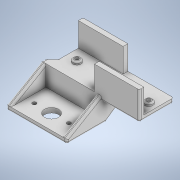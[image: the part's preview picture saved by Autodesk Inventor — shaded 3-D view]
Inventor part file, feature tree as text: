
AUTODESK INVENTOR PART (.ipt)
format: ipt  version: 2022 (Build 260153000, 153)  size: 325,120 bytes
history: native  units: in
note: dims shown in document units (in); Inventor stores cm internally (conversion verified against a paired STEP export)
features: extrude x9, sketch x9, chamfer x2, fillet x1
ambient origin geometry x8: Origin, YZ Plane, XZ Plane, XY Plane, X Axis, Y Axis, Z Axis, Center Point
bodies: Solid1 (feature_tree)
feature tree (21):
  extrude  "Extrusion1"  Depth=1.4331in
  extrude  "Extrusion2"  Depth=0.1969in
  extrude  "Extrusion3"  Depth=0.1969in
  extrude  "Extrusion5"  Depth=1.0in TaperAngle=0.0deg
  chamfer  "Chamfer1"  Distance=0.1181in
  extrude  "Extrusion6"  Depth=0.3937in
  extrude  "Extrusion7"  Depth=0.3937in
  extrude  "Extrusion8"  Depth=0.3937in
  chamfer  "Chamfer2"  Distance=0.0984in
  extrude  "Extrusion9"  Depth=0.0787in TaperAngle=45.0deg
  fillet  "Fillet2"  Radius=2.5197in
  extrude  "Extrusion10"  Depth=0.1969in
  sketch  "Sketch1"  dims[d0=3.7795in d1=1.4331in]
  sketch  "Sketch2"  dims[d2=0.1969in d3=0.0in d4=1.8701in]
  sketch  "Sketch3"  dims[d5=0.1969in d6=1.8701in]
  sketch  "Sketch5"  dims[d7=0.1969in d8=1.0in d9=0.0in]
  sketch  "Sketch6"  dims[d10=0.3406in]
  sketch  "Sketch7"  dims[d11=0.3406in]
  sketch  "Sketch8"  dims[d12=0.3406in]
  sketch  "Sketch9"  dims[d13=0.3406in d14=0.1181in d15=0.0in]
  sketch  "Sketch10"  dims[d22=0.2362in d23=0.2362in d24=0.2362in d25=0.2362in d26=0.0984in d27=0.0in d28=0.0591in d29=0.0787in d30=45.0deg d33=2.5197in d34=0.1969in d35=0.1969in d36=0.1969in d37=0.1969in d38=0.8504in d39=0.0in d40=0.1969in d41=0.0in d42=0.1969in d43=0.1969in d44=0.1969in d45=1.4508in d46=0.0in d47=3.937in d48=0.0in d49=0.315in d50=0.0787in d51=45.0deg d52=0.5906in d53=0.1575in d54=0.1575in d55=0.2362in d56=0.0in d57=0.0787in d58=0.1575in d59=0.1575in d60=0.1575in d61=0.1575in d62=0.3937in d63=0.0in d64=0.0197in d65=0.0344in]
